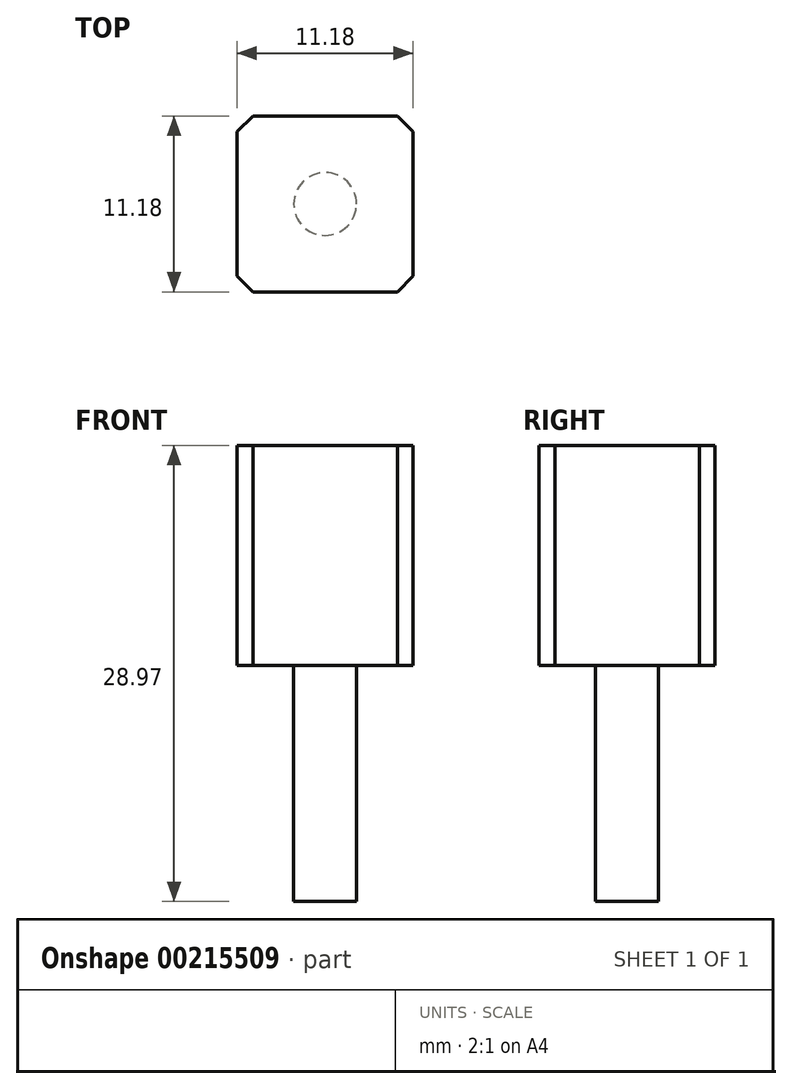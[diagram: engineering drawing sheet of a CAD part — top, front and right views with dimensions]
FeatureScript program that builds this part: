
annotation { "Feature Type Name" : "Feature", "Feature Type Description" : "" }
export const myFeature = defineFeature(function(context is Context, id is Id, definition is map)
    precondition{}
    {
        {
            var Q0;
            Q0=qCreatedBy(makeId("Top.planeOp"),FACE);
            var sketch = newSketch(context, id + "F0", { "sketchPlane" : qUnion([Q0])});
            skLineSegment(sketch, "E0.bottom", {"start": v(5.59, -5.59) * mm, "end": v(-5.59, -5.59) * mm});
            skLineSegment(sketch, "E0.top", {"start": v(5.59, 5.59) * mm, "end": v(-5.59, 5.59) * mm});
            skLineSegment(sketch, "E0.left", {"start": v(5.59, -5.59) * mm, "end": v(5.59, 5.59) * mm});
            skLineSegment(sketch, "E0.right", {"start": v(-5.59, -5.59) * mm, "end": v(-5.59, 5.59) * mm});
            skPoint(sketch, "E0.middle", {"position": v(0, 0) * mm});
            skSolve(sketch);
        }
        {
            var Q0;
            Q0=makeQuery(id+"F0.imprint","IMPRINT",FACE,{"disambiguationData":[TD([[makeQuery(id+"F0.imprint","IMPRINT",EDGE,{"derivedFrom":sQuery(id+"F0.wireOp",EDGE,"E0.bottom")}),-1.0]])]});
            extrude(context, id + "F1", {"entities" : qUnion([Q0]), "depth" : 13.97 * mm});
        }
        {
            var Q0;
            Q0=makeQuery(id+"F1.opExtrude","SWEPT_EDGE",EDGE,{"disambiguationData":[OSD([sQuery(id+"F0.wireOp",EDGE,"E0.top"),sQuery(id+"F0.wireOp",EDGE,"E0.left")])]});
            var Q1;
            Q1=makeQuery(id+"F1.opExtrude","SWEPT_EDGE",EDGE,{"disambiguationData":[OSD([sQuery(id+"F0.wireOp",EDGE,"E0.bottom"),sQuery(id+"F0.wireOp",EDGE,"E0.left")])]});
            var Q2;
            Q2=makeQuery(id+"F1.opExtrude","SWEPT_EDGE",EDGE,{"disambiguationData":[OSD([sQuery(id+"F0.wireOp",EDGE,"E0.bottom"),sQuery(id+"F0.wireOp",EDGE,"E0.right")])]});
            var Q3;
            Q3=makeQuery(id+"F1.opExtrude","SWEPT_EDGE",EDGE,{"disambiguationData":[OSD([sQuery(id+"F0.wireOp",EDGE,"E0.top"),sQuery(id+"F0.wireOp",EDGE,"E0.right")])]});
            chamfer(context, id + "F2", {"entities" : qUnion([Q0, Q1, Q2, Q3]), "width" : 1 * mm, "tangentPropagation" : true});
        }
        {
            var Q0;
            Q0=makeQuery(id+"F1.opExtrude","CAP_FACE",FACE,{"disambiguationData":[OSD([sQuery(id+"F0.wireOp",EDGE,"E0.bottom"),sQuery(id+"F0.wireOp",EDGE,"E0.top"),sQuery(id+"F0.wireOp",EDGE,"E0.left"),sQuery(id+"F0.wireOp",EDGE,"E0.right")])],"isStart":true});
            var sketch = newSketch(context, id + "F3", { "sketchPlane" : qUnion([Q0])});
            skCircle(sketch, "E1", {"center": v(0, 0) * mm, "radius": 2 * mm});
            skSolve(sketch);
        }
        {
            var Q0;
            Q0=makeQuery(id+"F3.imprint","IMPRINT",FACE,{"disambiguationData":[TD([[makeQuery(id+"F3.imprint","IMPRINT",EDGE,{"derivedFrom":sQuery(id+"F3.wireOp",EDGE,"E1")}),1.0]])]});
            var Q1;
            Q1=sQuery(id+"F3.wireOp",EDGE,"E1");
            extrude(context, id + "F4", {"entities" : qUnion([Q0]), "operationType" : NewBodyOperationType.ADD, "surfaceEntities" : qUnion([Q1]), "depth" : 15 * mm});
        }
    });
